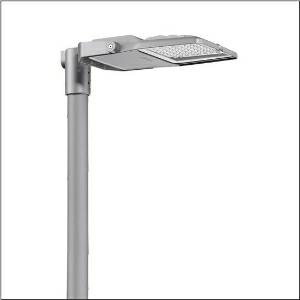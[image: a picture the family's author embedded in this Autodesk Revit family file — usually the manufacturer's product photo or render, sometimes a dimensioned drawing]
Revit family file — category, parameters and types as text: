
# Revit family: floodlight_fl_21_mini___pl43_5xa7772d2a3a_e9c8
name_source: partatom
category: Lighting Fixtures
units: mm (PartAtom-declared; Revit-internal decimal feet)

## family parameters
Cut with Voids When Loaded = No
Host = Face
Light Source = No
Part Type = Normal
Room Calculation Point = No
Round Connector Dimension = Use Diameter
Shared = No

## types (1)
- --- (1 x LED, 18290 lm, 143 W, 3000K)
    Apparent Load = 143 VA
    CIE Flux Codes = 27 78 99 100 100
    Color Rendering = 70
    Color Temperature = 3000K
    Default Elevation = 1800 mm
    Description = Floodlight FL 21 mini, floodlight, primary light control with lens, of PMMA, primary optical cover: protective disc, of toughened safety glass, transparent, light distribution: PL43, light emission: direct distribution, installation type: surface-mounted, LED, High Power LED, rated luminous flux: 18.290lm, luminous efficacy: 128lm/W, light colour: 730, colour temperature: 3000K, control gear: ECG iQ, control: Auto-Match, Temp-Guard, Night-Set, Smart-Wire, Desk-Remote (wireless, voltage-free reading and setting of iQ features in the workshop via application-optimized NFC function/RFID function), optimised constant luminous flux control (CLO 2.0), Light-Fading, Lumen-Switch, with terminal, 6-pole, mains connection: 220..240V, AC, 50/60Hz, start of lifetime: 143W, end of lifetime: 152W, reduction: 61W, luminaire housing, of diecast aluminium, powder-coated, Siteco® metallic grey (DB 702S), corrosivity category C5 according to DIN EN ISO 12944, mast bracket, of steel, galvanised, powder-coated, protection rating (complete): IP66, insulation class (complete): insulation class II (safety insulation), certification: CE, ENEC, VDE, protection symbol: D, impact resistance: IK08, permissible operating ambient temperature: -40..+40°C, permissible operating ambient temperature for outdoor applications: -40..+50°C, standard: DIN EN 12944, packaging unit: 1 piece

Light Distribution: PL43
    Height = 70 mm
    Lamp = 1 x LED
    Lamp Light Flux = 18290 lm
    Lamp Power = 143 W
    Lamp count = 1
    Length = 485 mm
    Luminous efficacy = 128 lm/W
    Manufacturer = Siteco
    ModVariant = No
    Model = 5XA7772D2A3A
    Number of Poles = 1
    OnlyDefault = Yes
    Power Factor = 1
    Product Name = Floodlight FL 21 mini | PL43
    Product group = floodlight | pylon top
    ProductGroupID = 6101
    Protection Class = Protection class II
    Protection Degree = IP 66
    RLX_Detail_Level = 1
    RlxData = <blob elided: 101273 chars, md5=32776d11>
    Socket = socket
    Standby Power = 0 W
    System Light Flux = 18290 lm
    System Power = 143 W
    Type Comments = factory setting: luminous flux: 100 % | dim-lin: 254 | 730 mA
    Type Image = l_1007125.jpg
    URL = http://relux.com
    VarID = @adj_072811
    Voltage = 0 V
    Weight = 0.00 kg
    Width = 337 mm

## geometry (parser evidence)
native form markers: Blend x4, Sweep x11
no freeform markers — native parametric forms only
